# Revit family: r2018_videomax_sm
name_source: partatom
category: Устройства связи
revit_build: Autodesk Revit 2018 (Build: 20181011_1500(x64)
units: mm (PartAtom-declared; Revit-internal decimal feet)

## family parameters
Общий = Нет
Основа = Грань
При загрузке вырезать с полостями = Нет
Размер круглого соединителя = Использовать диаметр
Сохранять ориентацию аннотаций = Да
Тип детали = Нормальный
Точка расчета площади = Нет

## types (1)
- sm
    ADSK_Версия Revit = 2018
    ADSK_Версия семейства = v1
    ADSK_Единица измерения = шт.
    ADSK_Код изделия = ТУ 26.20.15-002-37165186-2020
    ADSK_Количество = 1
    ADSK_Коэффициент мощности = 0.96
    ADSK_Марка = VIDEOMAX-sm
    ADSK_Наименование = Видеосервер VIDEOMAX-sm
    ADSK_Напряжение = 230 В
    ADSK_Номинальная мощность = 0 В·А
    ADSK_Ток = 0 А
    Material = Черный
    URL = https://www.videomax-server.ru
    Высота = 233 мм
    Глубина = 220 мм
    Изготовитель = ООО «Видеомакс»
    Изображение типоразмера = sm.jpg
    Количество IP-камер = 0
    Количество входов 9-36V = 1
    Количество интерфейсов Gigabit LAN, шт = 2
    Максимальная мощность БП, Вт = 0
    Максимальная потребляемая мощность Вт = 0
    Максимальное тепловыделение, BTU/h = 0
    Отметка по умолчанию = 2600 мм
    Стоимость = 0 $
    Указания по монтажу = Для настольного или настенного размещения. Специальные монтажные аксессуары не требуются.
    Ширина = 233 мм
